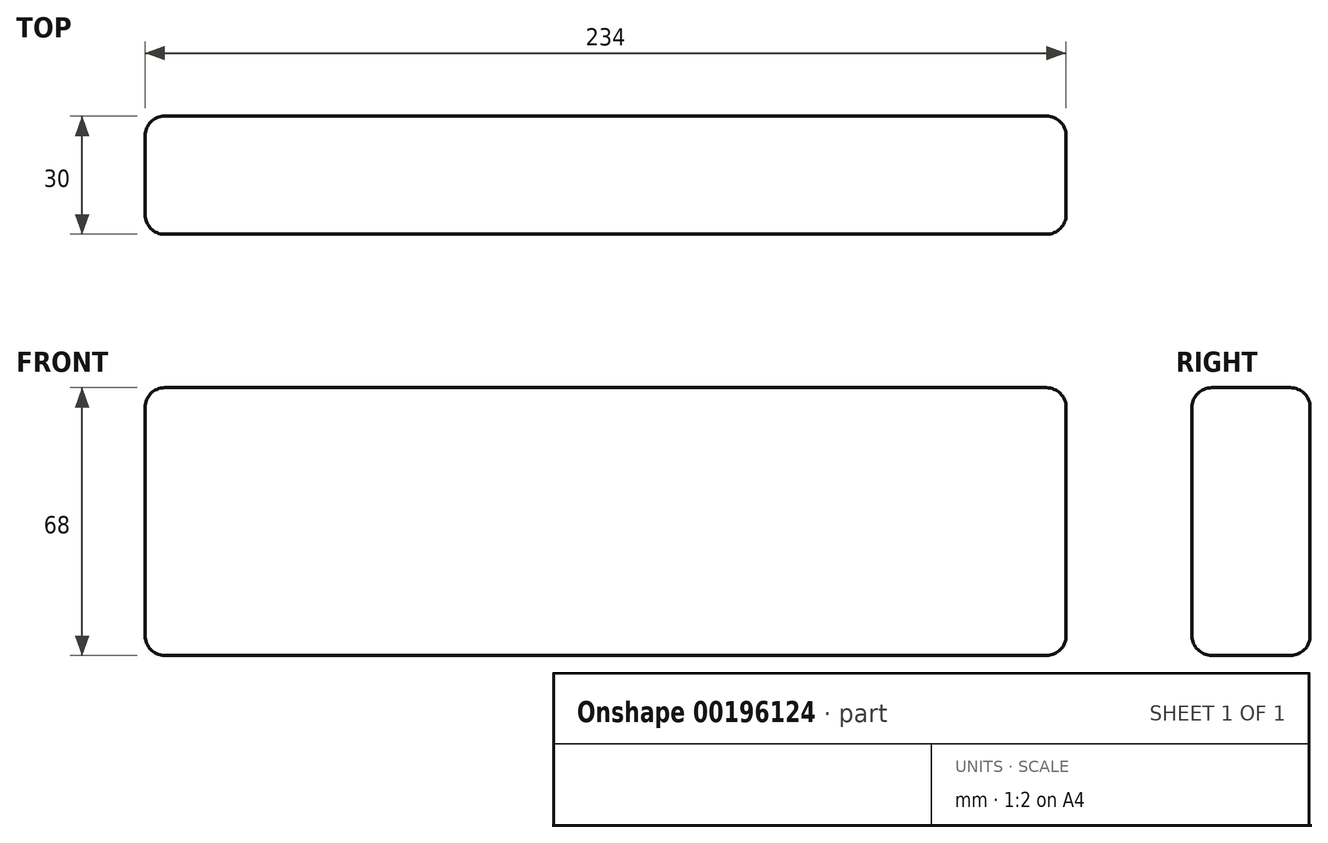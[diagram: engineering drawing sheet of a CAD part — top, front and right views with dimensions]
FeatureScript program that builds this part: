
annotation { "Feature Type Name" : "Feature", "Feature Type Description" : "" }
export const myFeature = defineFeature(function(context is Context, id is Id, definition is map)
    precondition{}
    {
        {
            var Q0;
            Q0=qCreatedBy(makeId("Front.planeOp"),FACE);
            var sketch = newSketch(context, id + "F0", { "sketchPlane" : qUnion([Q0])});
            skLineSegment(sketch, "E0.bottom", {"start": v(117, -34) * mm, "end": v(-117, -34) * mm});
            skLineSegment(sketch, "E0.top", {"start": v(117, 34) * mm, "end": v(-117, 34) * mm});
            skLineSegment(sketch, "E0.left", {"start": v(117, -34) * mm, "end": v(117, 34) * mm});
            skLineSegment(sketch, "E0.right", {"start": v(-117, -34) * mm, "end": v(-117, 34) * mm});
            skPoint(sketch, "E0.middle", {"position": v(0, 0) * mm});
            skSolve(sketch);
        }
        {
            var Q0;
            Q0 = qSketchRegion(id + "F0", true);
            extrude(context, id + "F1", {"entities" : qUnion([Q0]), "depth" : 30 * mm});
        }
        {
            var Q0;
            Q0=makeQuery(id+"F1.opExtrude","SWEPT_FACE",FACE,{"disambiguationData":[OSD([sQuery(id+"F0.wireOp",EDGE,"E0.top")])]});
            var Q1;
            Q1=makeQuery(id+"F1.opExtrude","SWEPT_FACE",FACE,{"disambiguationData":[OSD([sQuery(id+"F0.wireOp",EDGE,"E0.right")])]});
            var Q2;
            Q2=makeQuery(id+"F1.opExtrude","CAP_FACE",FACE,{"disambiguationData":[OSD([sQuery(id+"F0.wireOp",EDGE,"E0.bottom"),sQuery(id+"F0.wireOp",EDGE,"E0.top"),sQuery(id+"F0.wireOp",EDGE,"E0.left"),sQuery(id+"F0.wireOp",EDGE,"E0.right")])],"isStart":true});
            var Q3;
            Q3=makeQuery(id+"F1.opExtrude","CAP_FACE",FACE,{"disambiguationData":[OSD([sQuery(id+"F0.wireOp",EDGE,"E0.bottom"),sQuery(id+"F0.wireOp",EDGE,"E0.top"),sQuery(id+"F0.wireOp",EDGE,"E0.left"),sQuery(id+"F0.wireOp",EDGE,"E0.right")])],"isStart":false});
            var Q4;
            Q4=makeQuery(id+"F1.opExtrude","SWEPT_FACE",FACE,{"disambiguationData":[OSD([sQuery(id+"F0.wireOp",EDGE,"E0.left")])]});
            fillet(context, id + "F2", {"entities" : qUnion([Q0, Q1, Q2, Q3, Q4]), "radius" : 5 * mm, "tangentPropagation" : true, "allowEdgeOverflow" : false});
        }
    });
